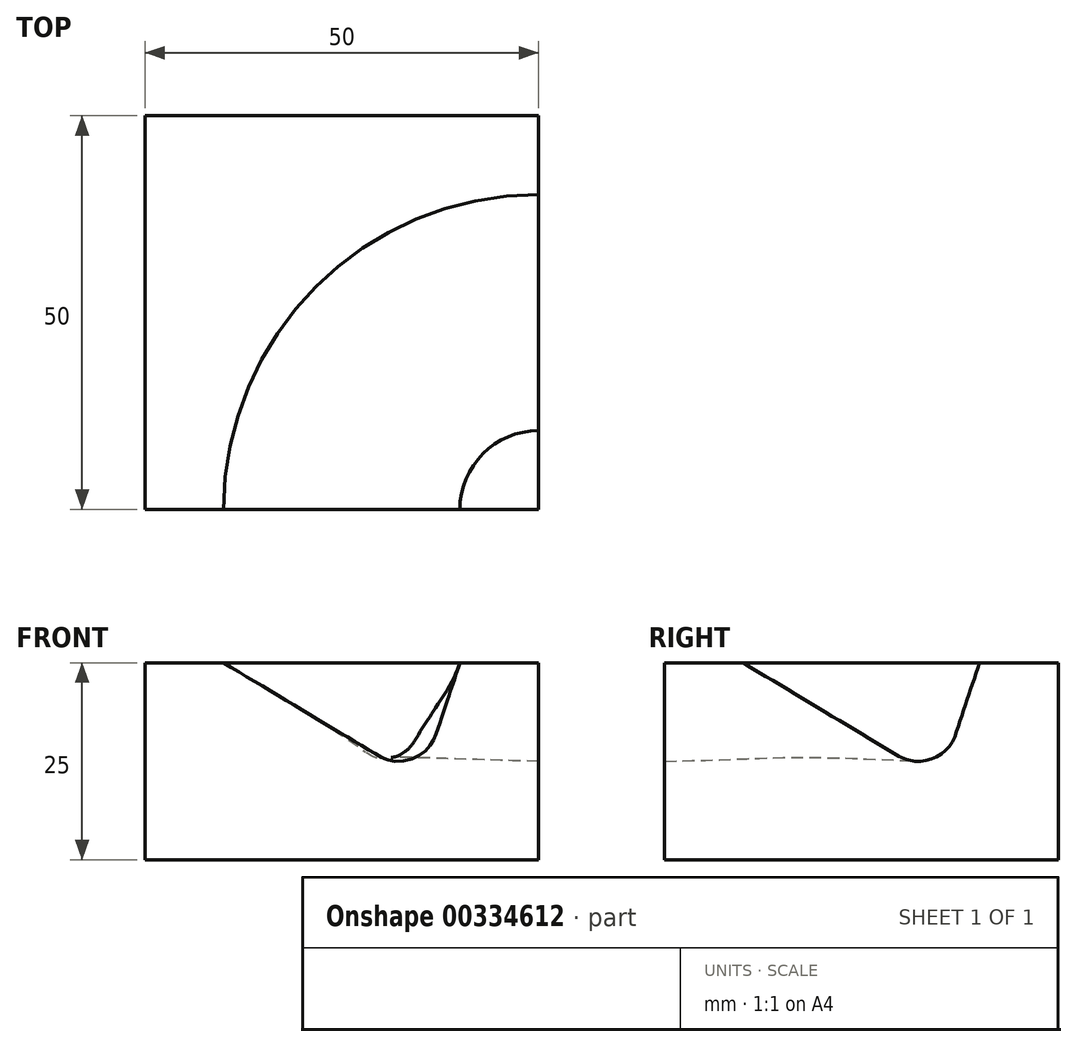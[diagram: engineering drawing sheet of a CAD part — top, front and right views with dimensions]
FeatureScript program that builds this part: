
annotation { "Feature Type Name" : "Feature", "Feature Type Description" : "" }
export const myFeature = defineFeature(function(context is Context, id is Id, definition is map)
    precondition{}
    {
        {
            var Q0;
            Q0=qCreatedBy(makeId("Top.planeOp"),FACE);
            var sketch = newSketch(context, id + "F0", { "sketchPlane" : qUnion([Q0])});
            skLineSegment(sketch, "E0.bottom", {"start": v(25, 25) * mm, "end": v(-25, 25) * mm});
            skLineSegment(sketch, "E0.top", {"start": v(25, -25) * mm, "end": v(-25, -25) * mm});
            skLineSegment(sketch, "E0.left", {"start": v(25, 25) * mm, "end": v(25, -25) * mm});
            skLineSegment(sketch, "E0.right", {"start": v(-25, 25) * mm, "end": v(-25, -25) * mm});
            skPoint(sketch, "E0.middle", {"position": v(0, 0) * mm});
            skSolve(sketch);
        }
        {
            var Q0;
            Q0 = qSketchRegion(id + "F0", true);
            extrude(context, id + "F1", {"entities" : qUnion([Q0]), "depth" : 25 * mm});
        }
        {
            var Q0;
            Q0=makeQuery(id+"F1.opExtrude","SWEPT_FACE",FACE,{"disambiguationData":[OSD([sQuery(id+"F0.wireOp",EDGE,"E0.top")])]});
            var sketch = newSketch(context, id + "F2", { "sketchPlane" : qUnion([Q0])});
            skLineSegment(sketch, "E1", {"start": v(-15, 25) * mm, "end": v(4.66, 13.2) * mm});
            skLineSegment(sketch, "E2", {"start": v(11.97, 15.91) * mm, "end": v(15, 25) * mm});
            skPoint(sketch, "E3.visualSharp", {"position": v(10, 10) * mm});
            skArc(sketch, "E3.filletArc", {"start": v(4.66, 13.2) * mm, "mid": v(8.96, 12.8) * mm, "end": v(11.97, 15.91) * mm});
            skSolve(sketch);
        }
        {
            var Q0;
            Q0=makeQuery(id+"F1.opExtrude","SWEPT_FACE",FACE,{"disambiguationData":[OSD([sQuery(id+"F0.wireOp",EDGE,"E0.left")])]});
            var sketch = newSketch(context, id + "F3", { "sketchPlane" : qUnion([Q0])});
            skLineSegment(sketch, "E4", {"start": v(-15, 25) * mm, "end": v(4.66, 13.2) * mm});
            skLineSegment(sketch, "E5", {"start": v(11.97, 15.91) * mm, "end": v(15, 25) * mm});
            skPoint(sketch, "E6.visualSharp", {"position": v(10, 10) * mm});
            skArc(sketch, "E6.filletArc", {"start": v(4.66, 13.2) * mm, "mid": v(8.96, 12.8) * mm, "end": v(11.97, 15.91) * mm});
            skSolve(sketch);
        }
        {
            var Q0;
            Q0=makeQuery(id+"F1.opExtrude","CAP_FACE",FACE,{"disambiguationData":[OSD([sQuery(id+"F0.wireOp",EDGE,"E0.bottom"),sQuery(id+"F0.wireOp",EDGE,"E0.top"),sQuery(id+"F0.wireOp",EDGE,"E0.left"),sQuery(id+"F0.wireOp",EDGE,"E0.right")])],"isStart":false});
            var sketch = newSketch(context, id + "F4", { "sketchPlane" : qUnion([Q0])});
            skCircle(sketch, "E7", {"center": v(25, -25) * mm, "radius": 10 * mm});
            skCircle(sketch, "E8", {"center": v(25, -25) * mm, "radius": 40 * mm});
            skSolve(sketch);
        }
        {
            var Q1;
            {var subQ0=sQuery(id+"F2.wireOp",EDGE,"E1");Q1=makeQuery(id+"F2.imprint","IMPRINT",FACE,{"disambiguationData":[TD([[makeQuery(id+"F2.imprint","IMPRINT",EDGE,{"derivedFrom":subQ0}),1.0]])]});}
            var Q2;
            {var subQ0=sQuery(id+"F3.wireOp",EDGE,"E4");Q2=makeQuery(id+"F3.imprint","IMPRINT",FACE,{"disambiguationData":[TD([[makeQuery(id+"F3.imprint","IMPRINT",EDGE,{"derivedFrom":subQ0}),1.0]])]});}
            var Q3;
            Q3=sQuery(id+"F4.wireOp",EDGE,"E8");
            var Q4;
            Q4=sQuery(id+"F4.wireOp",EDGE,"E7");
            loft(context, id + "F5", {"operationType" : NewBodyOperationType.REMOVE, "addGuides" : true, "sheetProfilesArray" : [{ "sheetProfileEntities" : qUnion([Q1]) }, { "sheetProfileEntities" : qUnion([Q2]) }], "guidesArray" : [{ "guideEntities" : qUnion([Q3]), "guideDerivativeType" : LoftGuideDerivativeType.DEFAULT, "guideDerivativeMagnitude" : 1 }, { "guideEntities" : qUnion([Q4]), "guideDerivativeType" : LoftGuideDerivativeType.DEFAULT, "guideDerivativeMagnitude" : 1 }]});
        }
    });
